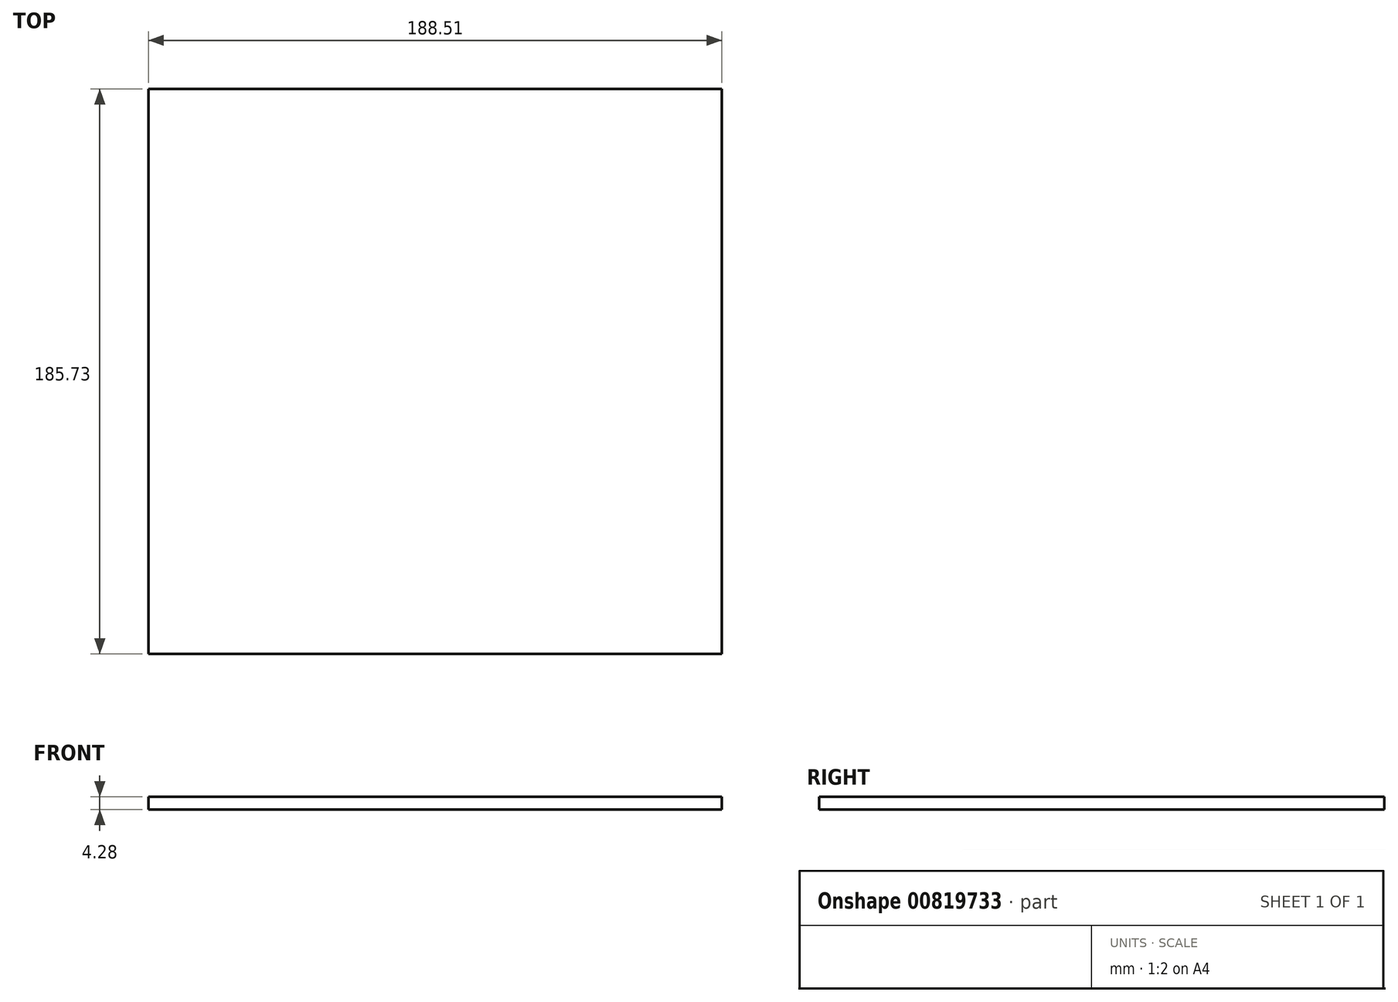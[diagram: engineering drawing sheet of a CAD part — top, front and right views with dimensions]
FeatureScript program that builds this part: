
annotation { "Feature Type Name" : "Feature", "Feature Type Description" : "" }
export const myFeature = defineFeature(function(context is Context, id is Id, definition is map)
    precondition{}
    {
        {
            var Q0;
            Q0=qCreatedBy(makeId("Top.planeOp"),FACE);
            var sketch = newSketch(context, id + "F0", { "sketchPlane" : qUnion([Q0])});
            skLineSegment(sketch, "E0.bottom", {"start": v(-93.87, 91.8) * mm, "end": v(94.64, 91.8) * mm});
            skLineSegment(sketch, "E0.top", {"start": v(-93.87, -93.92) * mm, "end": v(94.64, -93.92) * mm});
            skLineSegment(sketch, "E0.left", {"start": v(-93.87, 91.8) * mm, "end": v(-93.87, -93.92) * mm});
            skLineSegment(sketch, "E0.right", {"start": v(94.64, 91.8) * mm, "end": v(94.64, -93.92) * mm});
            skSolve(sketch);
        }
        {
            var Q0;
            Q0=makeQuery(id+"F0.imprint","IMPRINT",FACE,{"disambiguationData":[TD([[makeQuery(id+"F0.imprint","IMPRINT",EDGE,{"derivedFrom":sQuery(id+"F0.wireOp",EDGE,"E0.bottom")}),-1.0]])]});
            extrude(context, id + "F1", {"entities" : qUnion([Q0]), "depth" : 4.28 * mm, "offsetDistance" : 25.4 * mm});
        }
    });
